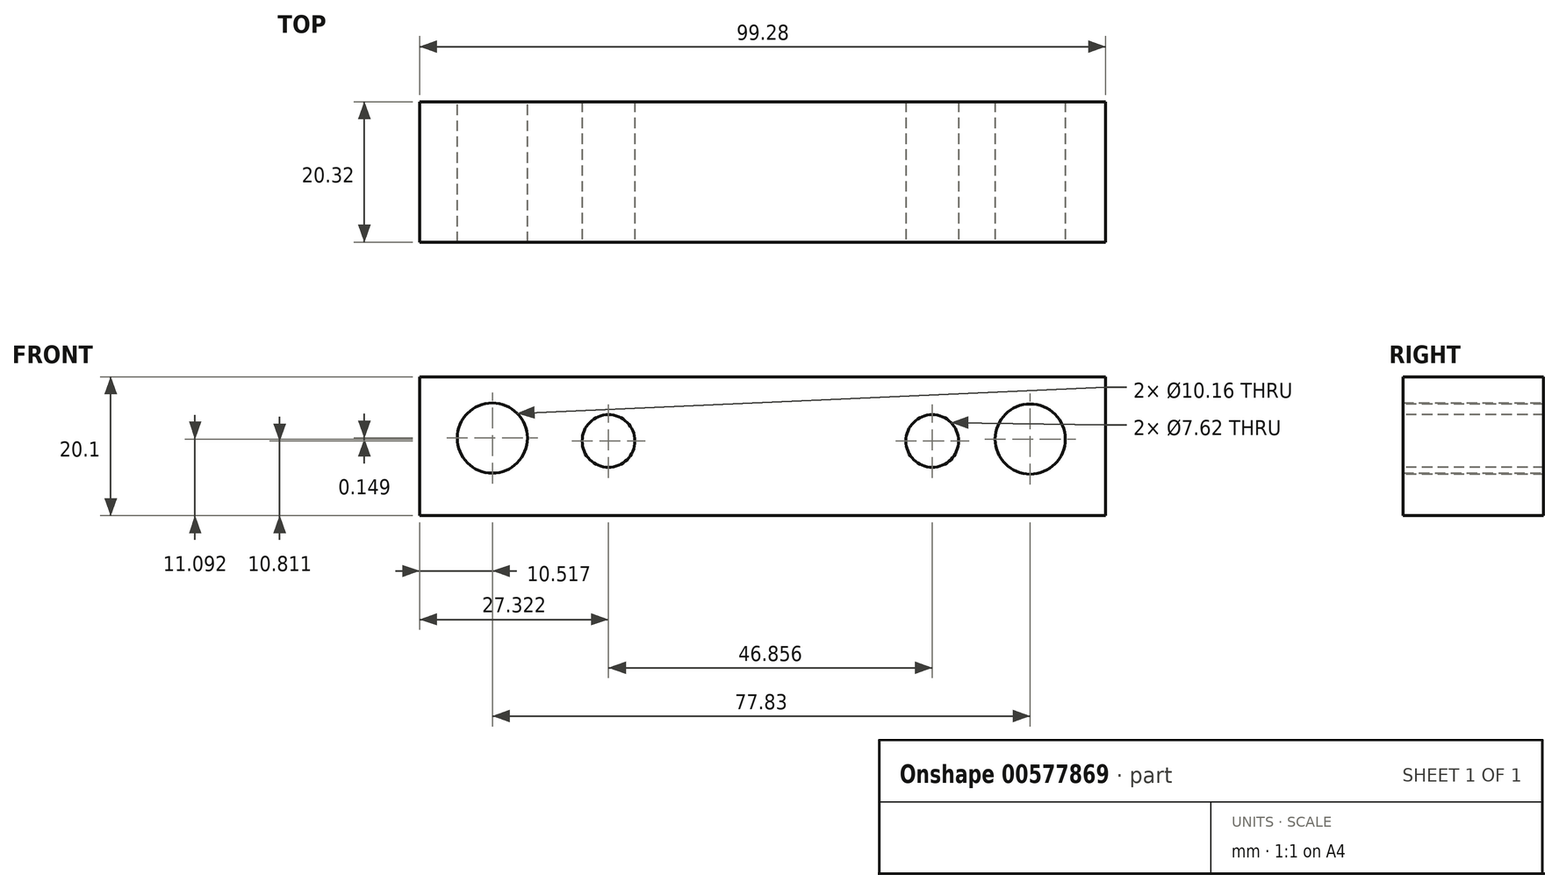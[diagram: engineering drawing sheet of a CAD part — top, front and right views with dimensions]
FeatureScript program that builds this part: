
annotation { "Feature Type Name" : "Feature", "Feature Type Description" : "" }
export const myFeature = defineFeature(function(context is Context, id is Id, definition is map)
    precondition{}
    {
        {
            var Q0;
            Q0=qCreatedBy(makeId("Front.planeOp"),FACE);
            var sketch = newSketch(context, id + "F0", { "sketchPlane" : qUnion([Q0])});
            skLineSegment(sketch, "E0.bottom", {"start": v(0, 0) * mm, "end": v(99.28, 0) * mm});
            skLineSegment(sketch, "E0.top", {"start": v(0, -20.1) * mm, "end": v(99.28, -20.1) * mm});
            skLineSegment(sketch, "E0.left", {"start": v(0, 0) * mm, "end": v(0, -20.1) * mm});
            skLineSegment(sketch, "E0.right", {"start": v(99.28, 0) * mm, "end": v(99.28, -20.1) * mm});
            skSolve(sketch);
        }
        {
            var Q0;
            Q0=makeQuery(id+"F0.imprint","IMPRINT",FACE,{"disambiguationData":[TD([[makeQuery(id+"F0.imprint","IMPRINT",EDGE,{"derivedFrom":sQuery(id+"F0.wireOp",EDGE,"E0.bottom")}),-1.0]])]});
            extrude(context, id + "F1", {"entities" : qUnion([Q0]), "depth" : 20.32 * mm, "offsetDistance" : 25.4 * mm});
        }
        {
            var Q0;
            Q0=qCreatedBy(makeId("Front.planeOp"),FACE);
            var sketch = newSketch(context, id + "F2", { "sketchPlane" : qUnion([Q0])});
            skPoint(sketch, "E1", {"position": v(10.52, -8.86) * mm});
            skSolve(sketch);
        }
        {
            var Q0;
            Q0=sQuery(id+"F2.wireOp",VERTEX,"E1");
            var Q1;
            Q1=makeQuery(id+"F1.opExtrude","SWEPT_BODY",BODY,{"disambiguationData":[OSD([sQuery(id+"F0.wireOp",EDGE,"E0.bottom"),sQuery(id+"F0.wireOp",EDGE,"E0.top"),sQuery(id+"F0.wireOp",EDGE,"E0.left"),sQuery(id+"F0.wireOp",EDGE,"E0.right")])]});
            hole(context, id + "F3", {"style" : HoleStyle.SIMPLE, "endStyle" : HoleEndStyle.THROUGH, "oppositeDirection" : true, "holeDiameter" : 10.16 * mm, "isTappedThrough" : true, "tappedDepth" : 12.7 * mm, "tapClearance" : 3, "locations" : qUnion([Q0]), "scope" : qUnion([Q1])});
        }
        {
            var Q0;
            Q0=makeQuery(id+"F1.opExtrude","CAP_FACE",FACE,{"disambiguationData":[OSD([sQuery(id+"F0.wireOp",EDGE,"E0.bottom"),sQuery(id+"F0.wireOp",EDGE,"E0.top"),sQuery(id+"F0.wireOp",EDGE,"E0.left"),sQuery(id+"F0.wireOp",EDGE,"E0.right")])],"isStart":false});
            var sketch = newSketch(context, id + "F4", { "sketchPlane" : qUnion([Q0])});
            skPoint(sketch, "E2", {"position": v(88.35, -9) * mm});
            skSolve(sketch);
        }
        {
            var Q0;
            Q0=sQuery(id+"F4.wireOp",VERTEX,"E2");
            var Q1;
            Q1=makeQuery(id+"F1.opExtrude","SWEPT_BODY",BODY,{"disambiguationData":[OSD([sQuery(id+"F0.wireOp",EDGE,"E0.bottom"),sQuery(id+"F0.wireOp",EDGE,"E0.top"),sQuery(id+"F0.wireOp",EDGE,"E0.left"),sQuery(id+"F0.wireOp",EDGE,"E0.right")])]});
            hole(context, id + "F5", {"style" : HoleStyle.SIMPLE, "endStyle" : HoleEndStyle.THROUGH, "holeDiameter" : 10.16 * mm, "isTappedThrough" : true, "tappedDepth" : 12.7 * mm, "tapClearance" : 3, "locations" : qUnion([Q0]), "scope" : qUnion([Q1])});
        }
        {
            var Q0;
            Q0=makeQuery(id+"F1.opExtrude","CAP_FACE",FACE,{"disambiguationData":[OSD([sQuery(id+"F0.wireOp",EDGE,"E0.bottom"),sQuery(id+"F0.wireOp",EDGE,"E0.top"),sQuery(id+"F0.wireOp",EDGE,"E0.left"),sQuery(id+"F0.wireOp",EDGE,"E0.right")])],"isStart":false});
            var sketch = newSketch(context, id + "F6", { "sketchPlane" : qUnion([Q0])});
            skPoint(sketch, "E3", {"position": v(27.32, -9.29) * mm});
            skPoint(sketch, "E4", {"position": v(74.18, -9.29) * mm});
            skSolve(sketch);
        }
        {
            var Q0;
            Q0=sQuery(id+"F6.wireOp",VERTEX,"E3");
            var Q1;
            Q1=sQuery(id+"F6.wireOp",VERTEX,"E4");
            var Q2;
            Q2=makeQuery(id+"F1.opExtrude","SWEPT_BODY",BODY,{"disambiguationData":[OSD([sQuery(id+"F0.wireOp",EDGE,"E0.bottom"),sQuery(id+"F0.wireOp",EDGE,"E0.top"),sQuery(id+"F0.wireOp",EDGE,"E0.left"),sQuery(id+"F0.wireOp",EDGE,"E0.right")])]});
            hole(context, id + "F7", {"style" : HoleStyle.SIMPLE, "endStyle" : HoleEndStyle.THROUGH, "holeDiameter" : 7.62 * mm, "isTappedThrough" : true, "tappedDepth" : 12.7 * mm, "tapClearance" : 3, "locations" : qUnion([Q0, Q1]), "scope" : qUnion([Q2])});
        }
    });
